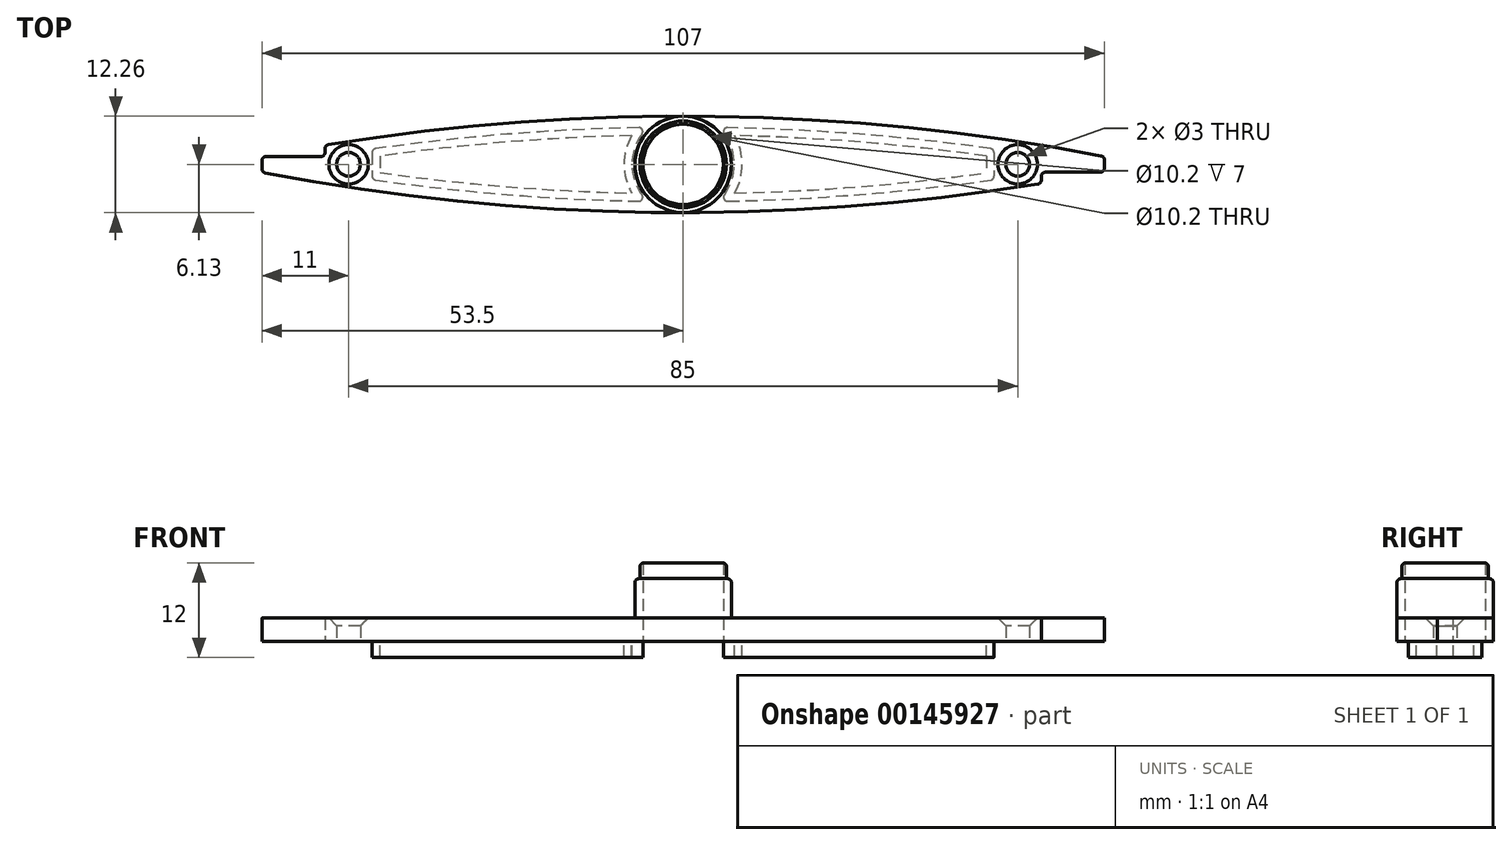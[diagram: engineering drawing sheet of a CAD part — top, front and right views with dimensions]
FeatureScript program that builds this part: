
annotation { "Feature Type Name" : "Feature", "Feature Type Description" : "" }
export const myFeature = defineFeature(function(context is Context, id is Id, definition is map)
    precondition{}
    {
        {
            var Q0;
            Q0=qCreatedBy(makeId("Top.planeOp"),FACE);
            var sketch = newSketch(context, id + "F0", { "sketchPlane" : qUnion([Q0])});
            skArc(sketch, "E0", {"start": v(-45.5, 2.43) * mm, "mid": v(4.06, 6.1) * mm, "end": v(53.5, 1) * mm});
            skArc(sketch, "E1", {"start": v(-53.5, -1) * mm, "mid": v(-4.06, -6.1) * mm, "end": v(45.5, -2.43) * mm});
            skLineSegment(sketch, "E2", {"start": v(-53.5, 1) * mm, "end": v(-53.5, -1) * mm});
            skLineSegment(sketch, "E3", {"start": v(53.5, 1) * mm, "end": v(53.5, -1) * mm});
            skCircle(sketch, "E4", {"center": v(0, 0) * mm, "radius": 5.1 * mm});
            skArc(sketch, "E5", {"start": v(-4.5, 4.69) * mm, "mid": v(-6.5, 0) * mm, "end": v(-4.5, -4.69) * mm});
            skArc(sketch, "E6.0", {"start": v(-39.5, 1.93) * mm, "mid": v(-22.04, 3.86) * mm, "end": v(-4.5, 4.69) * mm});
            skArc(sketch, "E7.0", {"start": v(-39.5, -1.93) * mm, "mid": v(-22.04, -3.86) * mm, "end": v(-4.5, -4.69) * mm});
            skLineSegment(sketch, "E8", {"start": v(-39.5, 1.93) * mm, "end": v(-39.5, -1.93) * mm});
            skLineSegment(sketch, "E9", {"start": v(39.5, 1.93) * mm, "end": v(39.5, -1.93) * mm});
            skLineSegment(sketch, "E10", {"start": v(53.5, -1) * mm, "end": v(45.5, -1) * mm});
            skLineSegment(sketch, "E11", {"start": v(45.5, -1) * mm, "end": v(45.5, -2.43) * mm});
            skLineSegment(sketch, "E12", {"start": v(-53.5, 1) * mm, "end": v(-45.5, 1) * mm});
            skLineSegment(sketch, "E13", {"start": v(-45.5, 1) * mm, "end": v(-45.5, 2.43) * mm});
            skArc(sketch, "E14.trimOffspring", {"start": v(4.5, 4.69) * mm, "mid": v(22.04, 3.86) * mm, "end": v(39.5, 1.93) * mm});
            skArc(sketch, "E15.trimOffspring", {"start": v(4.5, -4.69) * mm, "mid": v(6.5, 0) * mm, "end": v(4.5, 4.69) * mm});
            skArc(sketch, "E16.trimOffspring", {"start": v(4.5, -4.69) * mm, "mid": v(22.04, -3.86) * mm, "end": v(39.5, -1.93) * mm});
            skSolve(sketch);
        }
        {
            var Q0;
            Q0=qCreatedBy(makeId("Top.planeOp"),FACE);
            var sketch = newSketch(context, id + "F1", { "sketchPlane" : qUnion([Q0])});
            skArc(sketch, "E17.0", {"start": v(-53.5, -1) * mm, "mid": v(-4.06, -6.1) * mm, "end": v(45.5, -2.43) * mm});
            skLineSegment(sketch, "E17.1", {"start": v(-53.5, 1) * mm, "end": v(-53.5, -1) * mm});
            skLineSegment(sketch, "E17.2", {"start": v(-53.5, 1) * mm, "end": v(-45.5, 1) * mm});
            skLineSegment(sketch, "E17.3", {"start": v(-45.5, 1) * mm, "end": v(-45.5, 2.43) * mm});
            skArc(sketch, "E17.4", {"start": v(-45.5, 2.43) * mm, "mid": v(4.06, 6.1) * mm, "end": v(53.5, 1) * mm});
            skLineSegment(sketch, "E17.5", {"start": v(45.5, -1) * mm, "end": v(45.5, -2.43) * mm});
            skLineSegment(sketch, "E17.6", {"start": v(53.5, -1) * mm, "end": v(45.5, -1) * mm});
            skLineSegment(sketch, "E17.7", {"start": v(53.5, 1) * mm, "end": v(53.5, -1) * mm});
            skCircle(sketch, "E18.0", {"center": v(0, 0) * mm, "radius": 5.1 * mm});
            skSolve(sketch);
        }
        {
            var Q0;
            Q0 = qSketchRegion(id + "F1", true);
            extrude(context, id + "F2", {"entities" : qUnion([Q0]), "depth" : 3 * mm});
        }
        {
            var Q0;
            Q0=qCreatedBy(makeId("Top.planeOp"),FACE);
            var sketch = newSketch(context, id + "F3", { "sketchPlane" : qUnion([Q0])});
            skArc(sketch, "E19.0", {"start": v(-39.5, -1.93) * mm, "mid": v(-22.04, -3.86) * mm, "end": v(-4.5, -4.69) * mm});
            skArc(sketch, "E19.1", {"start": v(-39.5, 1.93) * mm, "mid": v(-22.04, 3.86) * mm, "end": v(-4.5, 4.69) * mm});
            skArc(sketch, "E19.2", {"start": v(-4.5, 4.69) * mm, "mid": v(-6.5, 0) * mm, "end": v(-4.5, -4.69) * mm});
            skArc(sketch, "E19.3", {"start": v(4.5, -4.69) * mm, "mid": v(6.5, 0) * mm, "end": v(4.5, 4.69) * mm});
            skArc(sketch, "E19.4", {"start": v(4.5, 4.69) * mm, "mid": v(22.04, 3.86) * mm, "end": v(39.5, 1.93) * mm});
            skArc(sketch, "E19.5", {"start": v(4.5, -4.69) * mm, "mid": v(22.04, -3.86) * mm, "end": v(39.5, -1.93) * mm});
            skLineSegment(sketch, "E19.6", {"start": v(39.5, 1.93) * mm, "end": v(39.5, -1.93) * mm});
            skLineSegment(sketch, "E19.7", {"start": v(-39.5, 1.93) * mm, "end": v(-39.5, -1.93) * mm});
            skArc(sketch, "E20.0", {"start": v(-38.5, 1.06) * mm, "mid": v(-22.56, 2.81) * mm, "end": v(-6.55, 3.65) * mm});
            skArc(sketch, "E21.0", {"start": v(-38.5, -1.06) * mm, "mid": v(-22.56, -2.81) * mm, "end": v(-6.55, -3.65) * mm});
            skLineSegment(sketch, "E22.0", {"start": v(-38.5, 1.06) * mm, "end": v(-38.5, -1.06) * mm});
            skArc(sketch, "E23.0", {"start": v(-6.55, 3.65) * mm, "mid": v(-7.5, 0) * mm, "end": v(-6.55, -3.65) * mm});
            skArc(sketch, "E24.0", {"start": v(6.55, 3.65) * mm, "mid": v(22.56, 2.81) * mm, "end": v(38.5, 1.06) * mm});
            skArc(sketch, "E25.0", {"start": v(6.55, -3.65) * mm, "mid": v(7.5, 0) * mm, "end": v(6.55, 3.65) * mm});
            skLineSegment(sketch, "E26.0", {"start": v(38.5, 1.06) * mm, "end": v(38.5, -1.06) * mm});
            skArc(sketch, "E27.0", {"start": v(6.55, -3.65) * mm, "mid": v(22.56, -2.81) * mm, "end": v(38.5, -1.06) * mm});
            skSolve(sketch);
        }
        {
            var Q0;
            Q0 = qSketchRegion(id + "F3", true);
            extrude(context, id + "F4", {"entities" : qUnion([Q0]), "operationType" : NewBodyOperationType.ADD, "oppositeDirection" : true, "depth" : 2 * mm});
        }
        {
            var Q0;
            Q0=makeQuery(id+"F2.opExtrude","CAP_FACE",FACE,{"disambiguationData":[OSD([sQuery(id+"F1.wireOp",EDGE,"E17.0"),sQuery(id+"F1.wireOp",EDGE,"E17.1"),sQuery(id+"F1.wireOp",EDGE,"E17.2"),sQuery(id+"F1.wireOp",EDGE,"E17.3"),sQuery(id+"F1.wireOp",EDGE,"E17.4"),sQuery(id+"F1.wireOp",EDGE,"E17.5"),sQuery(id+"F1.wireOp",EDGE,"E17.6"),sQuery(id+"F1.wireOp",EDGE,"E17.7"),sQuery(id+"F1.wireOp",EDGE,"E18.0")])],"isStart":false});
            var sketch = newSketch(context, id + "F5", { "sketchPlane" : qUnion([Q0])});
            skCircle(sketch, "E28", {"center": v(0, 0) * mm, "radius": 6.25 * mm});
            skCircle(sketch, "E29.0", {"center": v(0, 0) * mm, "radius": 5.1 * mm});
            skSolve(sketch);
        }
        {
            var Q0;
            {var subQ0=sQuery(id+"F1.wireOp",EDGE,"E17.2");var subQ1=sQuery(id+"F1.wireOp",EDGE,"E17.1");var subQ2=sQuery(id+"F1.wireOp",EDGE,"E17.3");var subQ3=sQuery(id+"F1.wireOp",EDGE,"E17.0");var subQ4=sQuery(id+"F1.wireOp",EDGE,"E17.4");Q0=makeQuery(id+"FQxeCIh0Ghwdrz1_1.boolean.opBoolean","SPLIT",FACE,{"disambiguationData":[TD([makeQuery(id+"F2.opExtrude","SWEPT_FACE",FACE,{"disambiguationData":[OSD([subQ1])]})])],"derivedFrom":makeQuery(id+"F2.opExtrude","CAP_FACE",FACE,{"disambiguationData":[OSD([subQ3,subQ1,subQ0,subQ2,subQ4,sQuery(id+"F1.wireOp",EDGE,"E17.5"),sQuery(id+"F1.wireOp",EDGE,"E17.6"),sQuery(id+"F1.wireOp",EDGE,"E17.7"),sQuery(id+"F1.wireOp",EDGE,"E18.0")])],"isStart":false})});}
            var sketch = newSketch(context, id + "F6", { "sketchPlane" : qUnion([Q0])});
            skCircle(sketch, "E30.0", {"center": v(0, 0) * mm, "radius": 5.1 * mm});
            skCircle(sketch, "E31", {"center": v(0, 0) * mm, "radius": 6.13 * mm});
            skSolve(sketch);
        }
        {
            var Q0;
            {var subQ0=makeQuery(id+"F2.opExtrude","CAP_EDGE",EDGE,{"disambiguationData":[OSD([sQuery(id+"F1.wireOp",EDGE,"E17.1")])],"isStart":false});Q0=makeQuery(id+"F6.imprint","IMPRINT",FACE,{"disambiguationData":[TD([[makeQuery(id+"F6.imprint","IMPRINT",EDGE,{"derivedFrom":subQ0}),1.0]])]});}
            var sketch = newSketch(context, id + "F7", { "sketchPlane" : qUnion([Q0])});
            skCircle(sketch, "E32.0", {"center": v(0, 0) * mm, "radius": 5.1 * mm});
            skCircle(sketch, "E33.0", {"center": v(0, 0) * mm, "radius": 6.13 * mm});
            skSolve(sketch);
        }
        {
            var Q0;
            Q0 = qSketchRegion(id + "F7", true);
            extrude(context, id + "F8", {"entities" : qUnion([Q0]), "depth" : 5 * mm});
        }
        {
            var Q0;
            Q0=makeQuery(id+"F8.opExtrude","CAP_FACE",FACE,{"disambiguationData":[OSD([sQuery(id+"F7.wireOp",EDGE,"E32.0"),sQuery(id+"F7.wireOp",EDGE,"Y6IsNL5e-9yLT-piMP-a285-wFKxheLaAHDe")])],"isStart":false});
            var sketch = newSketch(context, id + "F9", { "sketchPlane" : qUnion([Q0])});
            skCircle(sketch, "E34.0", {"center": v(0, 0) * mm, "radius": 5.1 * mm});
            skCircle(sketch, "E35", {"center": v(0, 0) * mm, "radius": 5.5 * mm});
            skSolve(sketch);
        }
        {
            var Q0;
            Q0 = qSketchRegion(id + "F9", true);
            extrude(context, id + "F10", {"entities" : qUnion([Q0]), "operationType" : NewBodyOperationType.ADD, "depth" : 2 * mm});
        }
        {
            var Q0;
            Q0=makeQuery(id+"F2.opExtrude","SWEPT_EDGE",EDGE,{"disambiguationData":[OSD([sQuery(id+"F1.wireOp",EDGE,"E17.6"),sQuery(id+"F1.wireOp",EDGE,"E17.7")])]});
            var Q1;
            Q1=makeQuery(id+"F2.opExtrude","SWEPT_EDGE",EDGE,{"disambiguationData":[OSD([sQuery(id+"F1.wireOp",EDGE,"E17.5"),sQuery(id+"F1.wireOp",EDGE,"E17.6")])]});
            var Q2;
            Q2=makeQuery(id+"F2.opExtrude","SWEPT_EDGE",EDGE,{"disambiguationData":[OSD([sQuery(id+"F1.wireOp",EDGE,"E17.3"),sQuery(id+"F1.wireOp",EDGE,"E17.4")])]});
            var Q3;
            Q3=makeQuery(id+"F2.opExtrude","SWEPT_EDGE",EDGE,{"disambiguationData":[OSD([sQuery(id+"F1.wireOp",EDGE,"E17.1"),sQuery(id+"F1.wireOp",EDGE,"E17.2")])]});
            var Q4;
            Q4=makeQuery(id+"F2.opExtrude","SWEPT_EDGE",EDGE,{"disambiguationData":[OSD([sQuery(id+"F1.wireOp",EDGE,"E17.0"),sQuery(id+"F1.wireOp",EDGE,"E17.1")])]});
            var Q5;
            Q5=makeQuery(id+"F4.opExtrude","SWEPT_EDGE",EDGE,{"disambiguationData":[OSD([sQuery(id+"F3.wireOp",EDGE,"E19.0"),sQuery(id+"F3.wireOp",EDGE,"E19.7")])]});
            var Q6;
            Q6=makeQuery(id+"F4.opExtrude","SWEPT_EDGE",EDGE,{"disambiguationData":[OSD([sQuery(id+"F3.wireOp",EDGE,"E19.1"),sQuery(id+"F3.wireOp",EDGE,"E19.7")])]});
            var Q7;
            Q7=makeQuery(id+"F4.opExtrude","SWEPT_EDGE",EDGE,{"disambiguationData":[OSD([sQuery(id+"F3.wireOp",EDGE,"E19.4"),sQuery(id+"F3.wireOp",EDGE,"E19.6")])]});
            var Q8;
            Q8=makeQuery(id+"F4.opExtrude","SWEPT_EDGE",EDGE,{"disambiguationData":[OSD([sQuery(id+"F3.wireOp",EDGE,"E19.5"),sQuery(id+"F3.wireOp",EDGE,"E19.6")])]});
            var Q9;
            Q9=makeQuery(id+"F4.opExtrude","SWEPT_EDGE",EDGE,{"disambiguationData":[OSD([sQuery(id+"F3.wireOp",EDGE,"E19.3"),sQuery(id+"F3.wireOp",EDGE,"E19.5")])]});
            var Q10;
            Q10=makeQuery(id+"F4.opExtrude","SWEPT_EDGE",EDGE,{"disambiguationData":[OSD([sQuery(id+"F3.wireOp",EDGE,"E19.0"),sQuery(id+"F3.wireOp",EDGE,"E19.2")])]});
            var Q11;
            Q11=makeQuery(id+"F4.opExtrude","SWEPT_EDGE",EDGE,{"disambiguationData":[OSD([sQuery(id+"F3.wireOp",EDGE,"E19.1"),sQuery(id+"F3.wireOp",EDGE,"E19.2")])]});
            var Q12;
            Q12=makeQuery(id+"F4.opExtrude","SWEPT_EDGE",EDGE,{"disambiguationData":[OSD([sQuery(id+"F3.wireOp",EDGE,"E19.3"),sQuery(id+"F3.wireOp",EDGE,"E19.4")])]});
            var Q13;
            Q13=makeQuery(id+"F8.opExtrude","CAP_EDGE",EDGE,{"disambiguationData":[OSD([sQuery(id+"F7.wireOp",EDGE,"E33.0")])],"isStart":false});
            var Q14;
            Q14=makeQuery(id+"F10.opExtrude","CAP_EDGE",EDGE,{"disambiguationData":[OSD([sQuery(id+"F9.wireOp",EDGE,"E35")])],"isStart":false});
            var Q15;
            Q15=makeQuery(id+"F2.opExtrude","SWEPT_EDGE",EDGE,{"disambiguationData":[OSD([sQuery(id+"F1.wireOp",EDGE,"E17.4"),sQuery(id+"F1.wireOp",EDGE,"E17.7")])]});
            var Q16;
            Q16=makeQuery(id+"F2.opExtrude","SWEPT_EDGE",EDGE,{"disambiguationData":[OSD([sQuery(id+"F1.wireOp",EDGE,"E17.0"),sQuery(id+"F1.wireOp",EDGE,"E17.5")])]});
            var Q17;
            Q17=makeQuery(id+"F2.opExtrude","SWEPT_EDGE",EDGE,{"disambiguationData":[OSD([sQuery(id+"F1.wireOp",EDGE,"E17.2"),sQuery(id+"F1.wireOp",EDGE,"E17.3")])]});
            fillet(context, id + "F11", {"entities" : qUnion([Q0, Q1, Q2, Q3, Q4, Q5, Q6, Q7, Q8, Q9, Q10, Q11, Q12, Q13, Q14, Q15, Q16, Q17]), "radius" : 0.5 * mm, "tangentPropagation" : true, "allowEdgeOverflow" : false});
        }
        {
            var Q0;
            Q0=qCreatedBy(makeId("Top.planeOp"),FACE);
            var sketch = newSketch(context, id + "F12", { "sketchPlane" : qUnion([Q0])});
            skCircle(sketch, "E36", {"center": v(-42.5, 0) * mm, "radius": 1.5 * mm});
            skCircle(sketch, "E37", {"center": v(42.5, 0) * mm, "radius": 1.5 * mm});
            skSolve(sketch);
        }
        {
            var Q0;
            Q0 = qSketchRegion(id + "F12", true);
            extrude(context, id + "F13", {"entities" : qUnion([Q0]), "operationType" : NewBodyOperationType.REMOVE, "endBound" : BoundingType.THROUGH_ALL, "depth" : 25 * mm});
        }
        {
            var Q0;
            Q0=makeQuery(id+"F13.boolean.opBoolean","INTERSECT",EDGE,{"derivedFrom":[makeQuery(id+"F2.opExtrude","CAP_FACE",FACE,{"disambiguationData":[OSD([sQuery(id+"F1.wireOp",EDGE,"E17.0"),sQuery(id+"F1.wireOp",EDGE,"E17.1"),sQuery(id+"F1.wireOp",EDGE,"E17.2"),sQuery(id+"F1.wireOp",EDGE,"E17.3"),sQuery(id+"F1.wireOp",EDGE,"E17.4"),sQuery(id+"F1.wireOp",EDGE,"E17.5"),sQuery(id+"F1.wireOp",EDGE,"E17.6"),sQuery(id+"F1.wireOp",EDGE,"E17.7"),sQuery(id+"F1.wireOp",EDGE,"E18.0")])],"isStart":false}),makeQuery(id+"F13.opExtrude","SWEPT_FACE",FACE,{"disambiguationData":[OSD([sQuery(id+"F12.wireOp",EDGE,"E36")])]})]});
            var Q1;
            Q1=makeQuery(id+"F13.boolean.opBoolean","INTERSECT",EDGE,{"derivedFrom":[makeQuery(id+"F2.opExtrude","CAP_FACE",FACE,{"disambiguationData":[OSD([sQuery(id+"F1.wireOp",EDGE,"E17.0"),sQuery(id+"F1.wireOp",EDGE,"E17.1"),sQuery(id+"F1.wireOp",EDGE,"E17.2"),sQuery(id+"F1.wireOp",EDGE,"E17.3"),sQuery(id+"F1.wireOp",EDGE,"E17.4"),sQuery(id+"F1.wireOp",EDGE,"E17.5"),sQuery(id+"F1.wireOp",EDGE,"E17.6"),sQuery(id+"F1.wireOp",EDGE,"E17.7"),sQuery(id+"F1.wireOp",EDGE,"E18.0")])],"isStart":false}),makeQuery(id+"F13.opExtrude","SWEPT_FACE",FACE,{"disambiguationData":[OSD([sQuery(id+"F12.wireOp",EDGE,"E37")])]})]});
            chamfer(context, id + "F14", {"entities" : qUnion([Q0, Q1]), "width" : 1 * mm, "tangentPropagation" : true});
        }
    });
